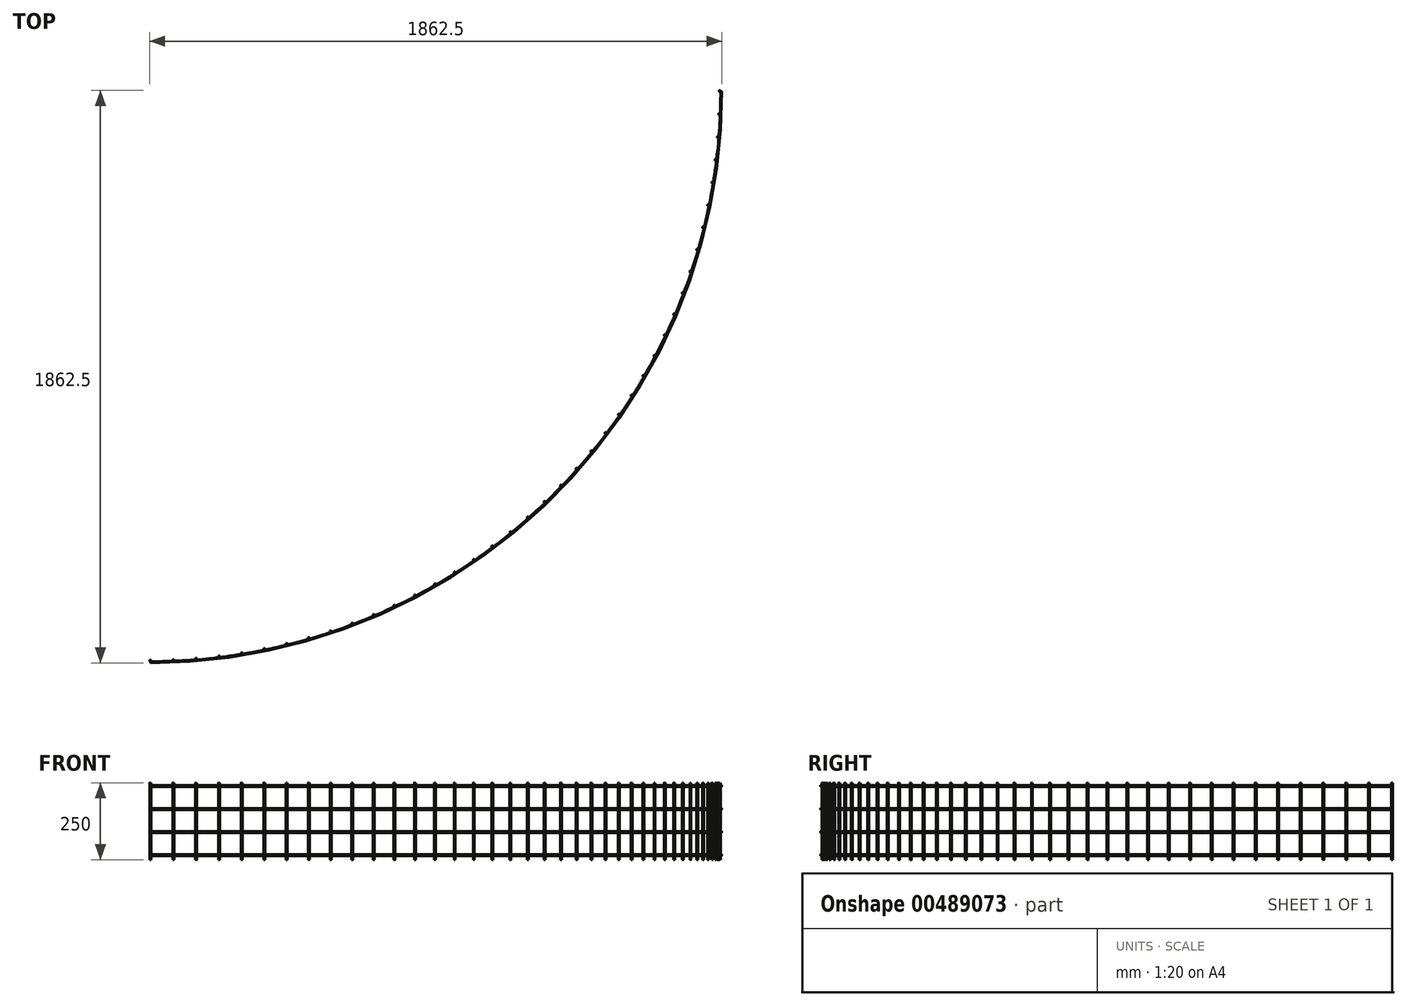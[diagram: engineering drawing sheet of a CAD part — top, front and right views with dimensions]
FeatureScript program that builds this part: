
annotation { "Feature Type Name" : "Feature", "Feature Type Description" : "" }
export const myFeature = defineFeature(function(context is Context, id is Id, definition is map)
    precondition{}
    {
        {
            var Q0;
            Q0=qCreatedBy(makeId("Top.planeOp"),FACE);
            var sketch = newSketch(context, id + "F0", { "sketchPlane" : qUnion([Q0])});
            skArc(sketch, "E0", {"start": v(0, -1852.5) * mm, "mid": v(1309.92, -1309.92) * mm, "end": v(1852.5, 0) * mm, "construction": true});
            skCircle(sketch, "E1", {"center": v(0, -1852.5) * mm, "radius": 2.5 * mm});
            skCircle(sketch, "E2.1.0", {"center": v(74.6, -1851) * mm, "radius": 2.5 * mm});
            skCircle(sketch, "E2.2.0", {"center": v(149.06, -1846.5) * mm, "radius": 2.5 * mm});
            skCircle(sketch, "E2.3.0", {"center": v(223.3, -1839) * mm, "radius": 2.5 * mm});
            skCircle(sketch, "E2.4.0", {"center": v(297.16, -1828.51) * mm, "radius": 2.5 * mm});
            skCircle(sketch, "E2.5.0", {"center": v(370.55, -1815.06) * mm, "radius": 2.5 * mm});
            skCircle(sketch, "E2.6.0", {"center": v(443.33, -1798.67) * mm, "radius": 2.5 * mm});
            skCircle(sketch, "E2.7.0", {"center": v(515.4, -1779.36) * mm, "radius": 2.5 * mm});
            skCircle(sketch, "E2.8.0", {"center": v(586.63, -1757.16) * mm, "radius": 2.5 * mm});
            skCircle(sketch, "E2.9.0", {"center": v(656.9, -1732.12) * mm, "radius": 2.5 * mm});
            skCircle(sketch, "E2.10.0", {"center": v(726.12, -1704.26) * mm, "radius": 2.5 * mm});
            skCircle(sketch, "E2.11.0", {"center": v(794.15, -1673.64) * mm, "radius": 2.5 * mm});
            skCircle(sketch, "E2.12.0", {"center": v(860.9, -1640.3) * mm, "radius": 2.5 * mm});
            skCircle(sketch, "E2.13.0", {"center": v(926.25, -1604.31) * mm, "radius": 2.5 * mm});
            skCircle(sketch, "E2.14.0", {"center": v(990.1, -1565.71) * mm, "radius": 2.5 * mm});
            skCircle(sketch, "E2.15.0", {"center": v(1052.34, -1524.58) * mm, "radius": 2.5 * mm});
            skCircle(sketch, "E2.16.0", {"center": v(1112.88, -1480.97) * mm, "radius": 2.5 * mm});
            skCircle(sketch, "E2.17.0", {"center": v(1171.6, -1434.96) * mm, "radius": 2.5 * mm});
            skCircle(sketch, "E2.18.0", {"center": v(1228.43, -1386.62) * mm, "radius": 2.5 * mm});
            skCircle(sketch, "E2.19.0", {"center": v(1283.27, -1336.03) * mm, "radius": 2.5 * mm});
            skCircle(sketch, "E2.20.0", {"center": v(1336.03, -1283.27) * mm, "radius": 2.5 * mm});
            skCircle(sketch, "E2.21.0", {"center": v(1386.62, -1228.43) * mm, "radius": 2.5 * mm});
            skCircle(sketch, "E2.22.0", {"center": v(1434.96, -1171.6) * mm, "radius": 2.5 * mm});
            skCircle(sketch, "E2.23.0", {"center": v(1480.97, -1112.88) * mm, "radius": 2.5 * mm});
            skCircle(sketch, "E2.24.0", {"center": v(1524.58, -1052.34) * mm, "radius": 2.5 * mm});
            skCircle(sketch, "E2.25.0", {"center": v(1565.71, -990.1) * mm, "radius": 2.5 * mm});
            skCircle(sketch, "E2.26.0", {"center": v(1604.31, -926.25) * mm, "radius": 2.5 * mm});
            skCircle(sketch, "E2.27.0", {"center": v(1640.3, -860.9) * mm, "radius": 2.5 * mm});
            skCircle(sketch, "E2.28.0", {"center": v(1673.64, -794.15) * mm, "radius": 2.5 * mm});
            skCircle(sketch, "E2.29.0", {"center": v(1704.26, -726.12) * mm, "radius": 2.5 * mm});
            skCircle(sketch, "E2.30.0", {"center": v(1732.12, -656.9) * mm, "radius": 2.5 * mm});
            skCircle(sketch, "E2.31.0", {"center": v(1757.16, -586.63) * mm, "radius": 2.5 * mm});
            skCircle(sketch, "E2.32.0", {"center": v(1779.36, -515.4) * mm, "radius": 2.5 * mm});
            skCircle(sketch, "E2.33.0", {"center": v(1798.67, -443.33) * mm, "radius": 2.5 * mm});
            skCircle(sketch, "E2.34.0", {"center": v(1815.06, -370.55) * mm, "radius": 2.5 * mm});
            skCircle(sketch, "E2.35.0", {"center": v(1828.51, -297.16) * mm, "radius": 2.5 * mm});
            skCircle(sketch, "E2.36.0", {"center": v(1839, -223.3) * mm, "radius": 2.5 * mm});
            skCircle(sketch, "E2.37.0", {"center": v(1846.5, -149.06) * mm, "radius": 2.5 * mm});
            skCircle(sketch, "E2.38.0", {"center": v(1851, -74.6) * mm, "radius": 2.5 * mm});
            skCircle(sketch, "E2.39.0", {"center": v(1852.5, 0) * mm, "radius": 2.5 * mm});
            skLineSegment(sketch, "E2.anchor1", {"start": v(0, 0) * mm, "end": v(0, -1852.5) * mm, "construction": true});
            skLineSegment(sketch, "E2.anchor2", {"start": v(0, 0) * mm, "end": v(1852.5, 0) * mm, "construction": true});
            skSolve(sketch);
        }
        {
            var Q0;
            Q0 = qSketchRegion(id + "F0", true);
            extrude(context, id + "F1", {"entities" : qUnion([Q0]), "depth" : 250 * mm, "symmetric" : true});
        }
        {
            var Q0;
            Q0=qCreatedBy(makeId("Right.planeOp"),FACE);
            var sketch = newSketch(context, id + "F2", { "sketchPlane" : qUnion([Q0])});
            skCircle(sketch, "E3", {"center": v(-1857.5, 115) * mm, "radius": 2.5 * mm});
            skCircle(sketch, "E4.0.1.0", {"center": v(-1857.5, 40) * mm, "radius": 2.5 * mm});
            skCircle(sketch, "E4.0.2.0", {"center": v(-1857.5, -35) * mm, "radius": 2.5 * mm});
            skCircle(sketch, "E4.0.3.0", {"center": v(-1857.5, -110) * mm, "radius": 2.5 * mm});
            skLineSegment(sketch, "E4.direction1", {"start": v(-1857.5, 100) * mm, "end": v(-1832.5, 100) * mm, "construction": true});
            skLineSegment(sketch, "E4.direction2", {"start": v(-1857.5, 100) * mm, "end": v(-1857.5, 25) * mm, "construction": true});
            skSolve(sketch);
        }
        {
            var Q0;
            Q0=qCreatedBy(makeId("Top.planeOp"),FACE);
            var Q1;
            Q1=sQuery(id+"F2.wireOp",VERTEX,"E3.center");
            cPlane(context, id + "F3", {"entities" : qUnion([Q0, Q1]), "cplaneType" : CPlaneType.PLANE_POINT, "offset" : 25 * mm, "width" : 150 * mm, "height" : 150 * mm});
        }
        {
            var Q0;
            Q0=qCreatedBy(id+"F3.planeOp",FACE);
            var sketch = newSketch(context, id + "F4", { "sketchPlane" : qUnion([Q0])});
            skArc(sketch, "E5", {"start": v(0, -1857.5) * mm, "mid": v(1313.45, -1313.45) * mm, "end": v(1857.5, 0) * mm});
            skSolve(sketch);
        }
        {
            var Q0;
            Q0 = qSketchRegion(id + "F2", true);
            var Q1;
            Q1=sQuery(id+"F4.wireOp",EDGE,"E5");
            sweep(context, id + "F5", {"profiles" : qUnion([Q0]), "path" : qUnion([Q1])});
        }
    });
